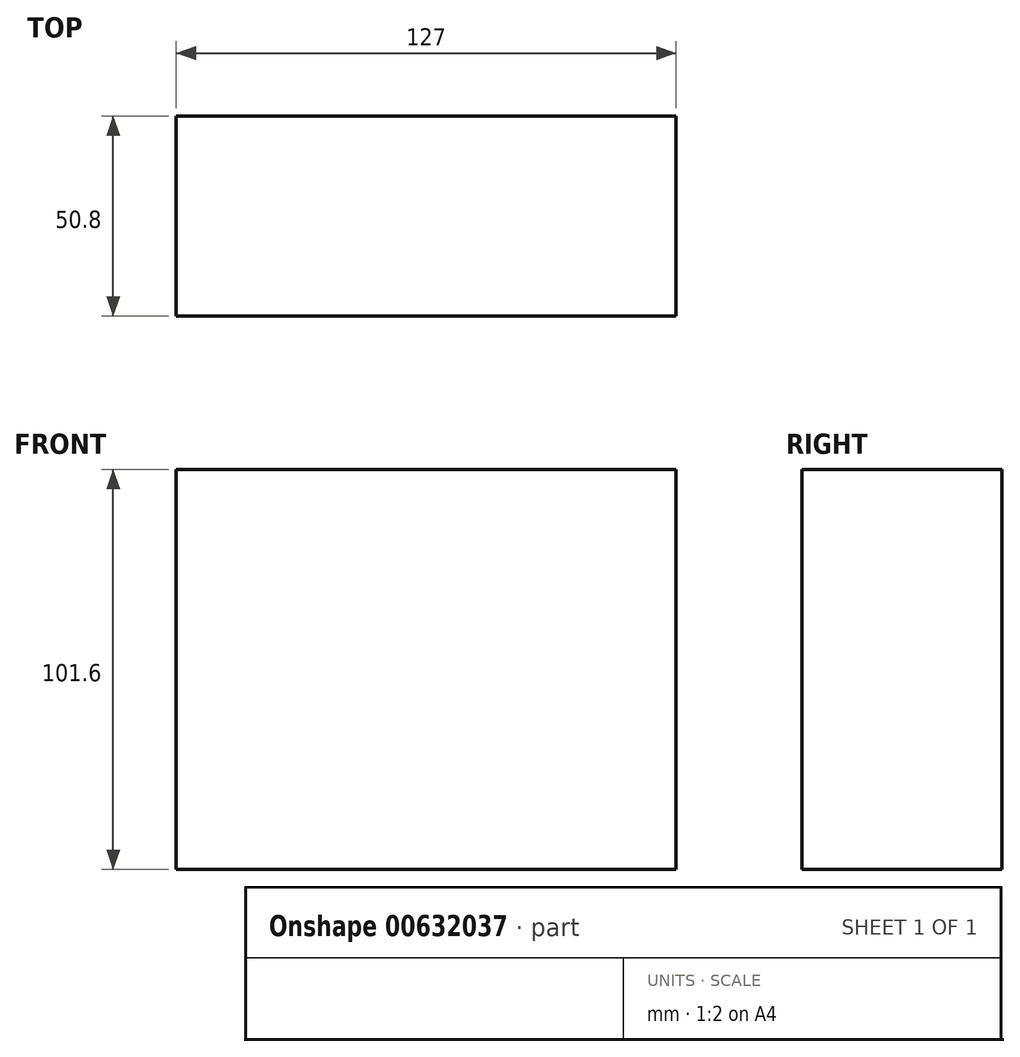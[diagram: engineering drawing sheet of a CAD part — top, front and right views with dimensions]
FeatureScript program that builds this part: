
annotation { "Feature Type Name" : "Feature", "Feature Type Description" : "" }
export const myFeature = defineFeature(function(context is Context, id is Id, definition is map)
    precondition{}
    {
        {
            var Q0;
            Q0=qCreatedBy(makeId("Front.planeOp"),FACE);
            var sketch = newSketch(context, id + "F0", { "sketchPlane" : qUnion([Q0])});
            skLineSegment(sketch, "E0.bottom", {"start": v(0, 0) * mm, "end": v(127, 0) * mm});
            skLineSegment(sketch, "E0.top", {"start": v(0, 101.6) * mm, "end": v(127, 101.6) * mm});
            skLineSegment(sketch, "E0.left", {"start": v(0, 0) * mm, "end": v(0, 101.6) * mm});
            skLineSegment(sketch, "E0.right", {"start": v(127, 0) * mm, "end": v(127, 101.6) * mm});
            skSolve(sketch);
        }
        {
            var Q0;
            Q0=makeQuery(id+"F0.imprint","IMPRINT",FACE,{"disambiguationData":[TD([[makeQuery(id+"F0.imprint","IMPRINT",EDGE,{"derivedFrom":sQuery(id+"F0.wireOp",EDGE,"E0.bottom")}),1.0]])]});
            extrude(context, id + "F1", {"entities" : qUnion([Q0]), "depth" : 50.8 * mm, "offsetDistance" : 25.4 * mm});
        }
    });
